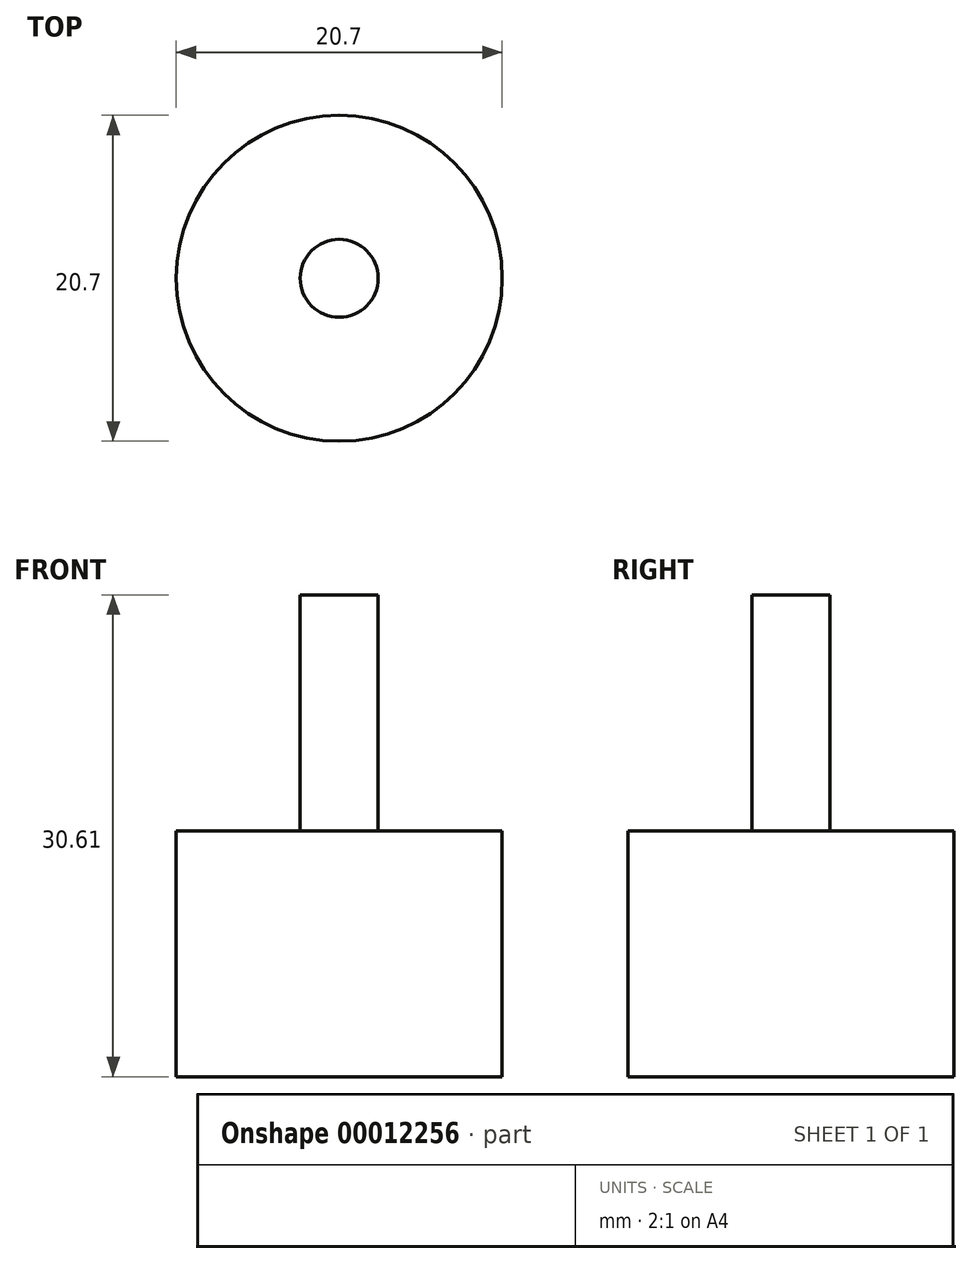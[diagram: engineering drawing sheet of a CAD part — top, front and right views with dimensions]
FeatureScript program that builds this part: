
annotation { "Feature Type Name" : "Feature", "Feature Type Description" : "" }
export const myFeature = defineFeature(function(context is Context, id is Id, definition is map)
    precondition{}
    {
        {
            var Q0;
            Q0=qCreatedBy(makeId("Top.planeOp"),FACE);
            var sketch = newSketch(context, id + "F0", { "sketchPlane" : qUnion([Q0])});
            skCircle(sketch, "E0", {"center": v(0, 0) * mm, "radius": 10.35 * mm});
            skSolve(sketch);
        }
        {
            var Q0;
            Q0=makeQuery(id+"F0.imprint","IMPRINT",FACE,{"disambiguationData":[TD([[makeQuery(id+"F0.imprint","IMPRINT",EDGE,{"derivedFrom":sQuery(id+"F0.wireOp",EDGE,"E0")}),1.0]])]});
            extrude(context, id + "F1", {"entities" : qUnion([Q0]), "depth" : 15.62 * mm});
        }
        {
            var Q0;
            Q0=makeQuery(id+"F1.opExtrude","CAP_FACE",FACE,{"disambiguationData":[OSD([sQuery(id+"F0.wireOp",EDGE,"E0")])],"isStart":false});
            var sketch = newSketch(context, id + "F2", { "sketchPlane" : qUnion([Q0])});
            skCircle(sketch, "E1", {"center": v(0, 0) * mm, "radius": 2.48 * mm});
            skSolve(sketch);
        }
        {
            var Q0;
            Q0 = qSketchRegion(id + "F2", true);
            extrude(context, id + "F3", {"entities" : qUnion([Q0]), "operationType" : NewBodyOperationType.ADD, "depth" : 15 * mm});
        }
    });
